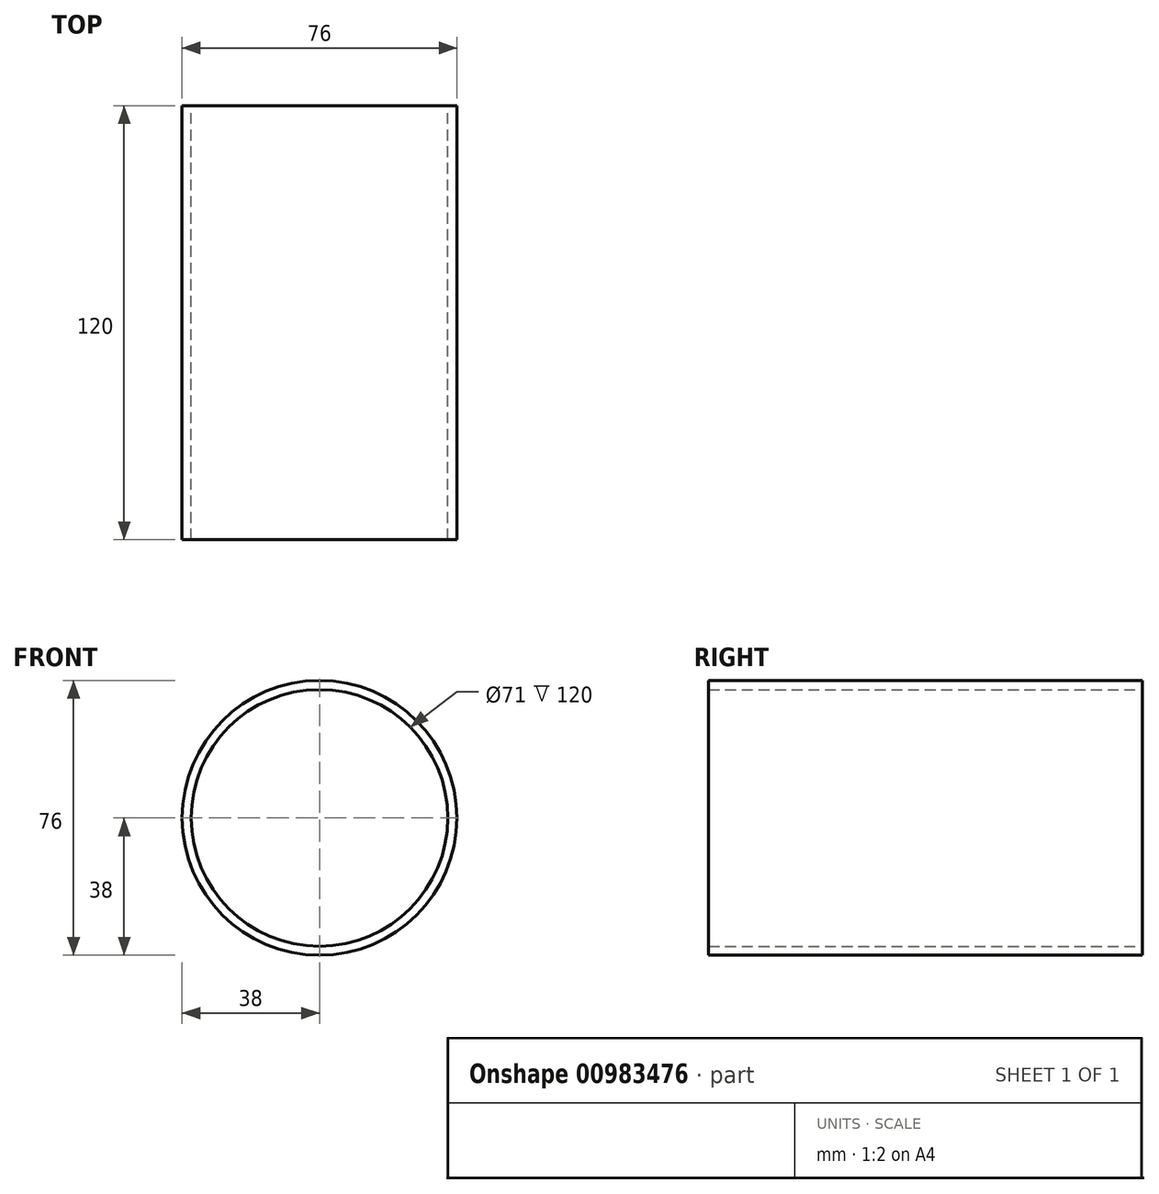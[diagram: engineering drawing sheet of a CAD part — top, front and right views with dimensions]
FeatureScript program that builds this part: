
annotation { "Feature Type Name" : "Feature", "Feature Type Description" : "" }
export const myFeature = defineFeature(function(context is Context, id is Id, definition is map)
    precondition{}
    {
        {
            var Q0;
            Q0=qCreatedBy(makeId("Front.planeOp"),FACE);
            var sketch = newSketch(context, id + "F0", { "sketchPlane" : qUnion([Q0])});
            skCircle(sketch, "E0", {"center": v(0, 0) * mm, "radius": 35.5 * mm});
            skCircle(sketch, "E1", {"center": v(0, 0) * mm, "radius": 38 * mm});
            skSolve(sketch);
        }
        {
            var Q0;
            Q0 = qSketchRegion(id + "F0", true);
            extrude(context, id + "F1", {"entities" : qUnion([Q0]), "depth" : 120 * mm, "offsetDistance" : 25 * mm});
        }
        {
            var Q0;
            Q0=qCreatedBy(makeId("Top.planeOp"),FACE);
            var sketch = newSketch(context, id + "F2", { "sketchPlane" : qUnion([Q0])});
            skLineSegment(sketch, "E2", {"start": v(0, 0) * mm, "end": v(-38, 0) * mm});
            skLineSegment(sketch, "E3.bottom", {"start": v(-38, 0) * mm, "end": v(38, 0) * mm});
            skLineSegment(sketch, "E3.top", {"start": v(-38, -120) * mm, "end": v(38, -120) * mm});
            skLineSegment(sketch, "E3.left", {"start": v(-38, 0) * mm, "end": v(-38, -120) * mm});
            skLineSegment(sketch, "E3.right", {"start": v(38, 0) * mm, "end": v(38, -120) * mm});
            skLineSegment(sketch, "E4", {"start": v(-38, -60) * mm, "end": v(38, -60) * mm, "construction": true});
            skLineSegment(sketch, "E5", {"start": v(0, 0) * mm, "end": v(0, -120) * mm, "construction": true});
            skCircle(sketch, "E6", {"center": v(0, -60) * mm, "radius": 16 * mm});
            skLineSegment(sketch, "E7.bottom", {"start": v(-15, -35) * mm, "end": v(20, -35) * mm});
            skLineSegment(sketch, "E7.top", {"start": v(-20, -85) * mm, "end": v(5, -85) * mm});
            skLineSegment(sketch, "E7.left", {"start": v(-25, -45) * mm, "end": v(-25, -80) * mm});
            skLineSegment(sketch, "E7.right", {"start": v(25, -40) * mm, "end": v(25, -65) * mm});
            skCircle(sketch, "E8", {"center": v(-18.9, -79.98) * mm, "radius": 1.25 * mm});
            skCircle(sketch, "E9", {"center": v(18.8, -39.94) * mm, "radius": 1.25 * mm});
            skPoint(sketch, "E10.visualSharp", {"position": v(-25, -35) * mm});
            skArc(sketch, "E10.filletArc", {"start": v(-15, -35) * mm, "mid": v(-22.07, -37.93) * mm, "end": v(-25, -45) * mm});
            skPoint(sketch, "E11.visualSharp", {"position": v(25, -35) * mm});
            skArc(sketch, "E11.filletArc", {"start": v(25, -40) * mm, "mid": v(23.54, -36.46) * mm, "end": v(20, -35) * mm});
            skPoint(sketch, "E12.visualSharp", {"position": v(-25, -85) * mm});
            skArc(sketch, "E12.filletArc", {"start": v(-25, -80) * mm, "mid": v(-23.54, -83.54) * mm, "end": v(-20, -85) * mm});
            skPoint(sketch, "E13.visualSharp", {"position": v(25, -85) * mm});
            skArc(sketch, "E13.filletArc", {"start": v(5, -85) * mm, "mid": v(19.14, -79.14) * mm, "end": v(25, -65) * mm});
            skSolve(sketch);
        }
        {
            var Q0;
            Q0=sQuery(id+"F2.wireOp",EDGE,"E13.filletArc");
            var Q1;
            Q1=sQuery(id+"F2.wireOp",EDGE,"E7.top");
            var Q2;
            Q2=sQuery(id+"F2.wireOp",EDGE,"E7.right");
            var Q3;
            Q3=sQuery(id+"F2.wireOp",EDGE,"E7.bottom");
            var Q4;
            Q4=sQuery(id+"F2.wireOp",EDGE,"E11.filletArc");
            var Q5;
            Q5=sQuery(id+"F2.wireOp",EDGE,"E10.filletArc");
            var Q6;
            Q6=sQuery(id+"F2.wireOp",EDGE,"E7.left");
            var Q7;
            Q7=sQuery(id+"F2.wireOp",EDGE,"E12.filletArc");
            var Q8;
            Q8=sQuery(id+"F2.wireOp",EDGE,"E6");
            extrude(context, id + "F3", {"bodyType" : ToolBodyType.SURFACE, "surfaceEntities" : qUnion([Q0, Q1, Q2, Q3, Q4, Q5, Q6, Q7, Q8]), "depth" : 50 * mm, "offsetDistance" : 25 * mm});
        }
        {
            var Q0;
            Q0=qCreatedBy(makeId("Top.planeOp"),FACE);
            cPlane(context, id + "F4", {"entities" : qUnion([Q0]), "cplaneType" : CPlaneType.OFFSET, "offset" : 50 * mm, "width" : 150 * mm, "height" : 150 * mm});
        }
    });
